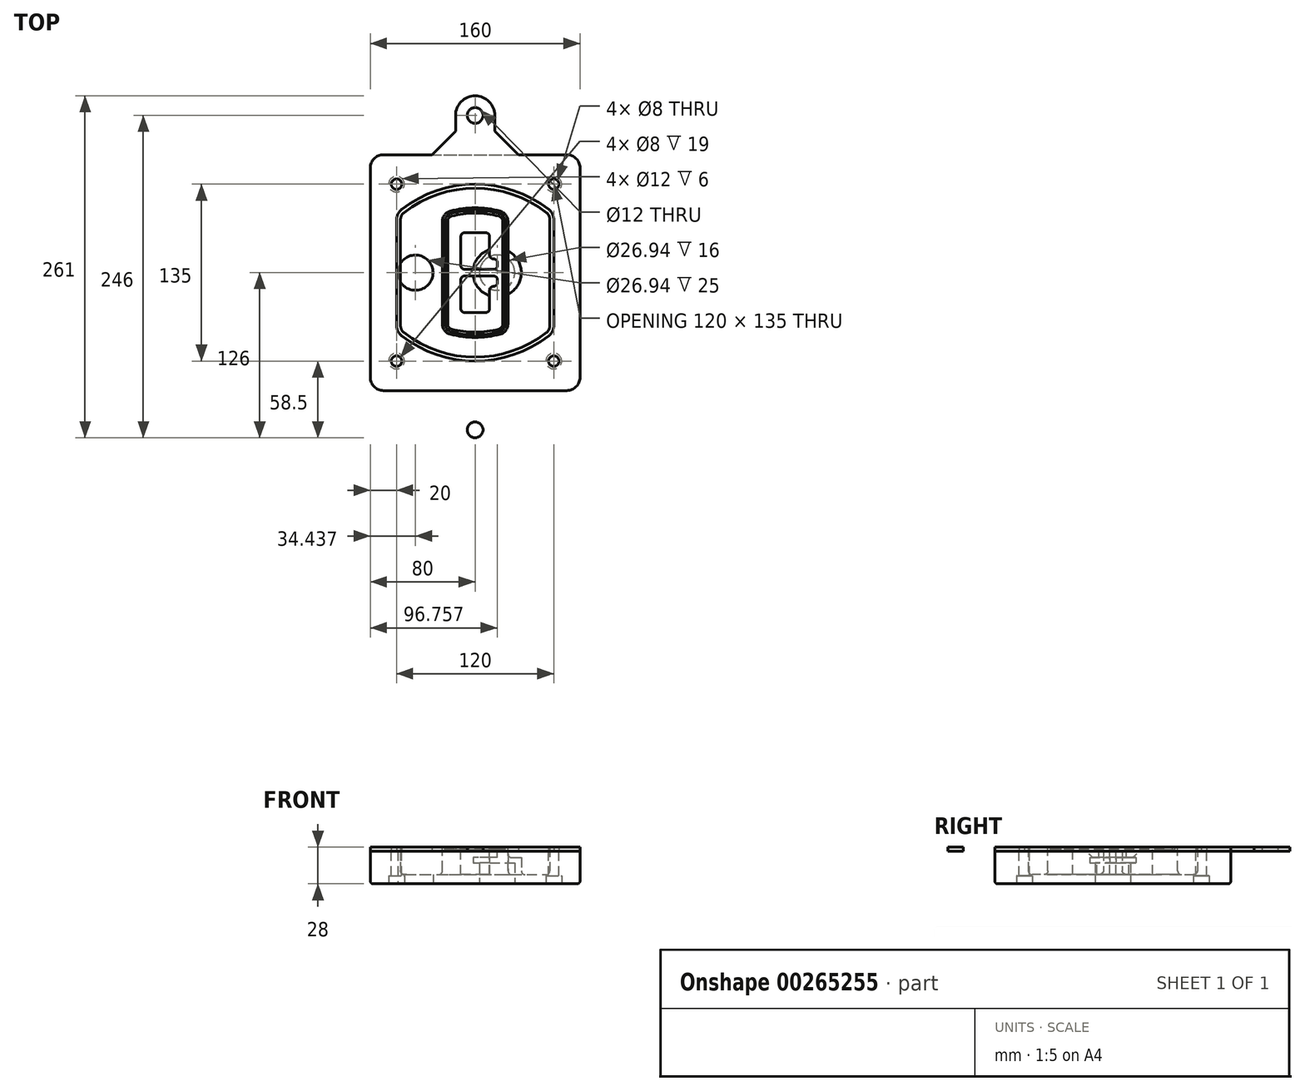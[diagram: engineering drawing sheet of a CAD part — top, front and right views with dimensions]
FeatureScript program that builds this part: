
annotation { "Feature Type Name" : "Feature", "Feature Type Description" : "" }
export const myFeature = defineFeature(function(context is Context, id is Id, definition is map)
    precondition{}
    {
        {
            var Q0;
            Q0=qCreatedBy(makeId("Top.planeOp"),FACE);
            var sketch = newSketch(context, id + "F0", { "sketchPlane" : qUnion([Q0])});
            skPoint(sketch, "E0.rect.middle", {"position": v(0, 0) * mm});
            skLineSegment(sketch, "E1.bottom", {"start": v(-70, -90) * mm, "end": v(70, -90) * mm});
            skLineSegment(sketch, "E1.top", {"start": v(-70, 90) * mm, "end": v(70, 90) * mm});
            skLineSegment(sketch, "E1.left", {"start": v(-80, -80) * mm, "end": v(-80, 80) * mm});
            skLineSegment(sketch, "E1.right", {"start": v(80, -80) * mm, "end": v(80, 80) * mm});
            skLineSegment(sketch, "E2", {"start": v(-80, 90) * mm, "end": v(80, -90) * mm, "construction": true});
            skLineSegment(sketch, "E3", {"start": v(80, 90) * mm, "end": v(-80, -90) * mm, "construction": true});
            skCircle(sketch, "E4", {"center": v(-60, 67.5) * mm, "radius": 4 * mm});
            skCircle(sketch, "E5", {"center": v(60, 67.5) * mm, "radius": 4 * mm});
            skCircle(sketch, "E6", {"center": v(60, -67.5) * mm, "radius": 4 * mm});
            skCircle(sketch, "E7", {"center": v(-60, -67.5) * mm, "radius": 4 * mm});
            skLineSegment(sketch, "E8", {"start": v(-60, 67.5) * mm, "end": v(60, 67.5) * mm, "construction": true});
            skLineSegment(sketch, "E9", {"start": v(60, 67.5) * mm, "end": v(60, -67.5) * mm, "construction": true});
            skLineSegment(sketch, "E10", {"start": v(60, -67.5) * mm, "end": v(-60, -67.5) * mm, "construction": true});
            skLineSegment(sketch, "E11", {"start": v(-60, -67.5) * mm, "end": v(-60, 67.5) * mm, "construction": true});
            skLineSegment(sketch, "E12", {"start": v(-60, 40.3) * mm, "end": v(-60, -40.3) * mm});
            skLineSegment(sketch, "E13", {"start": v(60, 40.3) * mm, "end": v(60, -40.3) * mm});
            skArc(sketch, "E14", {"start": v(56.15, 48.18) * mm, "mid": v(0, 67.5) * mm, "end": v(-56.15, 48.18) * mm});
            skArc(sketch, "E15", {"start": v(-56.15, -48.18) * mm, "mid": v(0, -67.5) * mm, "end": v(56.15, -48.18) * mm});
            skLineSegment(sketch, "E16", {"start": v(-60, 0) * mm, "end": v(60, 0) * mm, "construction": true});
            skPoint(sketch, "E17.visualSharp", {"position": v(-60, -45) * mm});
            skArc(sketch, "E17.filletArc", {"start": v(-60, -40.3) * mm, "mid": v(-58.99, -44.68) * mm, "end": v(-56.15, -48.18) * mm});
            skPoint(sketch, "E18.visualSharp", {"position": v(-60, 45) * mm});
            skArc(sketch, "E18.filletArc", {"start": v(-56.15, 48.18) * mm, "mid": v(-58.99, 44.68) * mm, "end": v(-60, 40.3) * mm});
            skPoint(sketch, "E19.visualSharp", {"position": v(60, 45) * mm});
            skArc(sketch, "E19.filletArc", {"start": v(60, 40.3) * mm, "mid": v(58.99, 44.68) * mm, "end": v(56.15, 48.18) * mm});
            skPoint(sketch, "E20.visualSharp", {"position": v(60, -45) * mm});
            skArc(sketch, "E20.filletArc", {"start": v(56.15, -48.18) * mm, "mid": v(58.99, -44.68) * mm, "end": v(60, -40.3) * mm});
            skPoint(sketch, "E21.visualSharp", {"position": v(-80, 90) * mm});
            skArc(sketch, "E21.filletArc", {"start": v(-70, 90) * mm, "mid": v(-77.07, 87.07) * mm, "end": v(-80, 80) * mm});
            skPoint(sketch, "E22.visualSharp", {"position": v(80, 90) * mm});
            skArc(sketch, "E22.filletArc", {"start": v(80, 80) * mm, "mid": v(77.07, 87.07) * mm, "end": v(70, 90) * mm});
            skPoint(sketch, "E23.visualSharp", {"position": v(80, -90) * mm});
            skArc(sketch, "E23.filletArc", {"start": v(70, -90) * mm, "mid": v(77.07, -87.07) * mm, "end": v(80, -80) * mm});
            skPoint(sketch, "E24.visualSharp", {"position": v(-80, -90) * mm});
            skArc(sketch, "E24.filletArc", {"start": v(-80, -80) * mm, "mid": v(-77.07, -87.07) * mm, "end": v(-70, -90) * mm});
            skArc(sketch, "E25.0", {"start": v(57, 40.3) * mm, "mid": v(56.3, 43.36) * mm, "end": v(54.3, 45.81) * mm});
            skLineSegment(sketch, "E25.1", {"start": v(57, 40.3) * mm, "end": v(57, -40.3) * mm});
            skArc(sketch, "E25.2", {"start": v(54.3, -45.81) * mm, "mid": v(56.3, -43.36) * mm, "end": v(57, -40.3) * mm});
            skArc(sketch, "E25.3", {"start": v(-54.3, -45.81) * mm, "mid": v(0, -64.5) * mm, "end": v(54.3, -45.81) * mm});
            skArc(sketch, "E25.4", {"start": v(-57, -40.3) * mm, "mid": v(-56.3, -43.36) * mm, "end": v(-54.3, -45.81) * mm});
            skArc(sketch, "E25.5", {"start": v(54.3, 45.81) * mm, "mid": v(0, 64.5) * mm, "end": v(-54.3, 45.81) * mm});
            skLineSegment(sketch, "E25.6", {"start": v(-57, 40.3) * mm, "end": v(-57, -40.3) * mm});
            skArc(sketch, "E25.7", {"start": v(-54.3, 45.81) * mm, "mid": v(-56.3, 43.36) * mm, "end": v(-57, 40.3) * mm});
            skArc(sketch, "E26.0", {"start": v(-58.62, 51.33) * mm, "mid": v(-62.58, 46.43) * mm, "end": v(-64, 40.3) * mm});
            skArc(sketch, "E26.1", {"start": v(58.62, 51.33) * mm, "mid": v(0, 71.5) * mm, "end": v(-58.62, 51.33) * mm});
            skArc(sketch, "E26.2", {"start": v(64, 40.3) * mm, "mid": v(62.58, 46.43) * mm, "end": v(58.62, 51.33) * mm});
            skLineSegment(sketch, "E26.3", {"start": v(64, 40.3) * mm, "end": v(64, -40.3) * mm});
            skArc(sketch, "E26.4", {"start": v(58.62, -51.33) * mm, "mid": v(62.58, -46.43) * mm, "end": v(64, -40.3) * mm});
            skLineSegment(sketch, "E26.5", {"start": v(-64, 40.3) * mm, "end": v(-64, -40.3) * mm});
            skArc(sketch, "E26.6", {"start": v(-58.62, -51.33) * mm, "mid": v(0, -71.5) * mm, "end": v(58.62, -51.33) * mm});
            skArc(sketch, "E26.7", {"start": v(-64, -40.3) * mm, "mid": v(-62.58, -46.43) * mm, "end": v(-58.62, -51.33) * mm});
            skSolve(sketch);
        }
        {
            var Q0;
            Q0=makeQuery(id+"F0.imprint","IMPRINT",FACE,{"disambiguationData":[TD([[makeQuery(id+"F0.imprint","IMPRINT",EDGE,{"derivedFrom":sQuery(id+"F0.wireOp",EDGE,"E1.bottom")}),1.0]])]});
            var Q1;
            Q1=makeQuery(id+"F0.imprint","IMPRINT",FACE,{"disambiguationData":[TD([[makeQuery(id+"F0.imprint","IMPRINT",EDGE,{"derivedFrom":sQuery(id+"F0.wireOp",EDGE,"E12")}),1.0]])]});
            var Q2;
            Q2=makeQuery(id+"F0.imprint","IMPRINT",FACE,{"disambiguationData":[TD([[makeQuery(id+"F0.imprint","IMPRINT",EDGE,{"derivedFrom":sQuery(id+"F0.wireOp",EDGE,"E25.0")}),1.0]])]});
            var Q3;
            Q3=makeQuery(id+"F0.imprint","IMPRINT",FACE,{"disambiguationData":[TD([[makeQuery(id+"F0.imprint","IMPRINT",EDGE,{"derivedFrom":sQuery(id+"F0.wireOp",EDGE,"E12")}),-1.0]])]});
            extrude(context, id + "F1", {"entities" : qUnion([Q0, Q1, Q2, Q3]), "oppositeDirection" : true, "depth" : 25 * mm});
        }
        {
            var Q0;
            Q0=makeQuery(id+"F0.imprint","IMPRINT",FACE,{"disambiguationData":[TD([[makeQuery(id+"F0.imprint","IMPRINT",EDGE,{"derivedFrom":sQuery(id+"F0.wireOp",EDGE,"E12")}),1.0]])]});
            extrude(context, id + "F2", {"entities" : qUnion([Q0]), "operationType" : NewBodyOperationType.ADD, "depth" : 3 * mm});
        }
        {
            var Q0;
            Q0=makeQuery(id+"F0.imprint","IMPRINT",FACE,{"disambiguationData":[TD([[makeQuery(id+"F0.imprint","IMPRINT",EDGE,{"derivedFrom":sQuery(id+"F0.wireOp",EDGE,"E25.0")}),1.0]])]});
            extrude(context, id + "F3", {"entities" : qUnion([Q0]), "operationType" : NewBodyOperationType.REMOVE, "oppositeDirection" : true, "depth" : 18 * mm});
        }
        {
            var Q0;
            Q0=makeQuery(id+"F2.opExtrude","CAP_FACE",FACE,{"disambiguationData":[OSD([sQuery(id+"F0.wireOp",EDGE,"E12"),sQuery(id+"F0.wireOp",EDGE,"E13"),sQuery(id+"F0.wireOp",EDGE,"E14"),sQuery(id+"F0.wireOp",EDGE,"E15"),sQuery(id+"F0.wireOp",EDGE,"E17.filletArc"),sQuery(id+"F0.wireOp",EDGE,"E18.filletArc"),sQuery(id+"F0.wireOp",EDGE,"E19.filletArc"),sQuery(id+"F0.wireOp",EDGE,"E20.filletArc"),sQuery(id+"F0.wireOp",EDGE,"E25.0"),sQuery(id+"F0.wireOp",EDGE,"E25.1"),sQuery(id+"F0.wireOp",EDGE,"E25.2"),sQuery(id+"F0.wireOp",EDGE,"E25.3"),sQuery(id+"F0.wireOp",EDGE,"E25.4"),sQuery(id+"F0.wireOp",EDGE,"E25.5"),sQuery(id+"F0.wireOp",EDGE,"E25.6"),sQuery(id+"F0.wireOp",EDGE,"E25.7")])],"isStart":false});
            var sketch = newSketch(context, id + "F4", { "sketchPlane" : qUnion([Q0])});
            skArc(sketch, "E27.0", {"start": v(-19.08, -46.97) * mm, "mid": v(0, -49.5) * mm, "end": v(19.08, -46.97) * mm});
            skArc(sketch, "E28.0", {"start": v(19.08, 46.97) * mm, "mid": v(0, 49.5) * mm, "end": v(-19.08, 46.97) * mm});
            skLineSegment(sketch, "E29", {"start": v(-25, 39.25) * mm, "end": v(-25, -39.25) * mm});
            skLineSegment(sketch, "E30", {"start": v(25, 39.25) * mm, "end": v(25, -39.25) * mm});
            skLineSegment(sketch, "E31", {"start": v(-25, 45.1) * mm, "end": v(25, 45.1) * mm, "construction": true});
            skLineSegment(sketch, "E32", {"start": v(-25, -45.1) * mm, "end": v(25, -45.1) * mm, "construction": true});
            skPoint(sketch, "E33.visualSharp", {"position": v(-25, 45.1) * mm});
            skArc(sketch, "E33.filletArc", {"start": v(-19.08, 46.97) * mm, "mid": v(-23.35, 44.11) * mm, "end": v(-25, 39.25) * mm});
            skPoint(sketch, "E34.visualSharp", {"position": v(25, 45.1) * mm});
            skArc(sketch, "E34.filletArc", {"start": v(25, 39.25) * mm, "mid": v(23.35, 44.11) * mm, "end": v(19.08, 46.97) * mm});
            skPoint(sketch, "E35.visualSharp", {"position": v(25, -45.1) * mm});
            skArc(sketch, "E35.filletArc", {"start": v(19.08, -46.97) * mm, "mid": v(23.35, -44.11) * mm, "end": v(25, -39.25) * mm});
            skPoint(sketch, "E36.visualSharp", {"position": v(-25, -45.1) * mm});
            skArc(sketch, "E36.filletArc", {"start": v(-25, -39.25) * mm, "mid": v(-23.35, -44.11) * mm, "end": v(-19.08, -46.97) * mm});
            skArc(sketch, "E37.0", {"start": v(54.3, 45.81) * mm, "mid": v(0, 64.5) * mm, "end": v(-54.3, 45.81) * mm});
            skArc(sketch, "E37.1", {"start": v(-54.3, 45.81) * mm, "mid": v(-56.3, 43.36) * mm, "end": v(-57, 40.3) * mm});
            skLineSegment(sketch, "E37.2", {"start": v(-57, 40.3) * mm, "end": v(-57, -40.3) * mm});
            skArc(sketch, "E37.3", {"start": v(-57, -40.3) * mm, "mid": v(-56.3, -43.36) * mm, "end": v(-54.3, -45.81) * mm});
            skArc(sketch, "E37.4", {"start": v(-54.3, -45.81) * mm, "mid": v(0, -64.5) * mm, "end": v(54.3, -45.81) * mm});
            skArc(sketch, "E37.5", {"start": v(54.3, -45.81) * mm, "mid": v(56.3, -43.36) * mm, "end": v(57, -40.3) * mm});
            skLineSegment(sketch, "E37.6", {"start": v(57, 40.3) * mm, "end": v(57, -40.3) * mm});
            skArc(sketch, "E37.7", {"start": v(57, 40.3) * mm, "mid": v(56.3, 43.36) * mm, "end": v(54.3, 45.81) * mm});
            skLineSegment(sketch, "E38.0", {"start": v(23, 39.25) * mm, "end": v(23, -39.25) * mm});
            skArc(sketch, "E38.1", {"start": v(18.56, -45.04) * mm, "mid": v(21.76, -42.9) * mm, "end": v(23, -39.25) * mm});
            skArc(sketch, "E38.2", {"start": v(-18.56, -45.04) * mm, "mid": v(0, -47.5) * mm, "end": v(18.56, -45.04) * mm});
            skArc(sketch, "E38.3", {"start": v(-23, -39.25) * mm, "mid": v(-21.76, -42.9) * mm, "end": v(-18.56, -45.04) * mm});
            skLineSegment(sketch, "E38.4", {"start": v(-23, 39.25) * mm, "end": v(-23, -39.25) * mm});
            skArc(sketch, "E38.5", {"start": v(23, 39.25) * mm, "mid": v(21.76, 42.9) * mm, "end": v(18.56, 45.04) * mm});
            skArc(sketch, "E38.6", {"start": v(-18.56, 45.04) * mm, "mid": v(-21.76, 42.9) * mm, "end": v(-23, 39.25) * mm});
            skArc(sketch, "E38.7", {"start": v(18.56, 45.04) * mm, "mid": v(0, 47.5) * mm, "end": v(-18.56, 45.04) * mm});
            skArc(sketch, "E39.0", {"start": v(21, 39.25) * mm, "mid": v(20.18, 41.68) * mm, "end": v(18.04, 43.1) * mm});
            skLineSegment(sketch, "E39.1", {"start": v(21, 39.25) * mm, "end": v(21, -39.25) * mm});
            skArc(sketch, "E39.2", {"start": v(18.04, -43.1) * mm, "mid": v(20.18, -41.68) * mm, "end": v(21, -39.25) * mm});
            skArc(sketch, "E39.3", {"start": v(-18.04, -43.1) * mm, "mid": v(0, -45.5) * mm, "end": v(18.04, -43.1) * mm});
            skArc(sketch, "E39.4", {"start": v(-21, -39.25) * mm, "mid": v(-20.18, -41.68) * mm, "end": v(-18.04, -43.1) * mm});
            skArc(sketch, "E39.5", {"start": v(18.04, 43.1) * mm, "mid": v(0, 45.5) * mm, "end": v(-18.04, 43.1) * mm});
            skLineSegment(sketch, "E39.6", {"start": v(-21, 39.25) * mm, "end": v(-21, -39.25) * mm});
            skArc(sketch, "E39.7", {"start": v(-18.04, 43.1) * mm, "mid": v(-20.18, 41.68) * mm, "end": v(-21, 39.25) * mm});
            skLineSegment(sketch, "E40", {"start": v(-25, 0) * mm, "end": v(25, 0) * mm, "construction": true});
            skLineSegment(sketch, "E41", {"start": v(-11, 5.5) * mm, "end": v(-11, 27.5) * mm});
            skLineSegment(sketch, "E42", {"start": v(-8, 30.5) * mm, "end": v(8, 30.5) * mm});
            skLineSegment(sketch, "E43", {"start": v(11, 27.5) * mm, "end": v(11, 13.5) * mm});
            skLineSegment(sketch, "E44", {"start": v(14, 10.5) * mm, "end": v(14, 10.5) * mm});
            skLineSegment(sketch, "E45", {"start": v(17, 7.5) * mm, "end": v(17, 5.5) * mm});
            skLineSegment(sketch, "E46", {"start": v(14, 2.5) * mm, "end": v(-8, 2.5) * mm});
            skPoint(sketch, "E47.visualSharp", {"position": v(-11, 30.5) * mm});
            skArc(sketch, "E47.filletArc", {"start": v(-8, 30.5) * mm, "mid": v(-10.12, 29.62) * mm, "end": v(-11, 27.5) * mm});
            skPoint(sketch, "E48.visualSharp", {"position": v(11, 30.5) * mm});
            skArc(sketch, "E48.filletArc", {"start": v(11, 27.5) * mm, "mid": v(10.12, 29.62) * mm, "end": v(8, 30.5) * mm});
            skPoint(sketch, "E49.visualSharp", {"position": v(11, 10.5) * mm});
            skArc(sketch, "E49.filletArc", {"start": v(11, 13.5) * mm, "mid": v(11.88, 11.38) * mm, "end": v(14, 10.5) * mm});
            skPoint(sketch, "E50.visualSharp", {"position": v(17, 10.5) * mm});
            skArc(sketch, "E50.filletArc", {"start": v(17, 7.5) * mm, "mid": v(16.12, 9.62) * mm, "end": v(14, 10.5) * mm});
            skPoint(sketch, "E51.visualSharp", {"position": v(17, 2.5) * mm});
            skArc(sketch, "E51.filletArc", {"start": v(14, 2.5) * mm, "mid": v(16.12, 3.38) * mm, "end": v(17, 5.5) * mm});
            skPoint(sketch, "E52.visualSharp", {"position": v(-11, 2.5) * mm});
            skArc(sketch, "E52.filletArc", {"start": v(-11, 5.5) * mm, "mid": v(-10.12, 3.38) * mm, "end": v(-8, 2.5) * mm});
            skLineSegment(sketch, "E53.0.MirrorCS", {"start": v(14, -2.5) * mm, "end": v(-8, -2.5) * mm});
            skArc(sketch, "E54.0.MirrorCS", {"start": v(-11, -5.5) * mm, "mid": v(-10.12, -3.38) * mm, "end": v(-8, -2.5) * mm});
            skLineSegment(sketch, "E55.0.MirrorCS", {"start": v(-11, -5.5) * mm, "end": v(-11, -27.5) * mm});
            skArc(sketch, "E56.0.MirrorCS", {"start": v(-8, -30.5) * mm, "mid": v(-10.12, -29.62) * mm, "end": v(-11, -27.5) * mm});
            skLineSegment(sketch, "E57.0.MirrorCS", {"start": v(-8, -30.5) * mm, "end": v(8, -30.5) * mm});
            skArc(sketch, "E58.0.MirrorCS", {"start": v(11, -27.5) * mm, "mid": v(10.12, -29.62) * mm, "end": v(8, -30.5) * mm});
            skLineSegment(sketch, "E59.0.MirrorCS", {"start": v(11, -27.5) * mm, "end": v(11, -13.5) * mm});
            skArc(sketch, "E60.0.MirrorCS", {"start": v(11, -13.5) * mm, "mid": v(11.88, -11.38) * mm, "end": v(14, -10.5) * mm});
            skArc(sketch, "E61.0.MirrorCS", {"start": v(17, -7.5) * mm, "mid": v(16.12, -9.62) * mm, "end": v(14, -10.5) * mm});
            skLineSegment(sketch, "E62.0.MirrorCS", {"start": v(17, -7.5) * mm, "end": v(17, -5.5) * mm});
            skArc(sketch, "E63.0.MirrorCS", {"start": v(14, -2.5) * mm, "mid": v(16.12, -3.38) * mm, "end": v(17, -5.5) * mm});
            skSolve(sketch);
        }
        {
            var Q0;
            Q0=makeQuery(id+"F4.imprint","IMPRINT",FACE,{"disambiguationData":[TD([[makeQuery(id+"F4.imprint","IMPRINT",EDGE,{"derivedFrom":sQuery(id+"F4.wireOp",EDGE,"E27.0")}),1.0]])]});
            var Q1;
            Q1=makeQuery(id+"F4.imprint","IMPRINT",FACE,{"disambiguationData":[TD([[makeQuery(id+"F4.imprint","IMPRINT",EDGE,{"derivedFrom":sQuery(id+"F4.wireOp",EDGE,"E38.0")}),-1.0]])]});
            var Q2;
            Q2=makeQuery(id+"F4.imprint","IMPRINT",FACE,{"disambiguationData":[TD([[makeQuery(id+"F4.imprint","IMPRINT",EDGE,{"derivedFrom":sQuery(id+"F4.wireOp",EDGE,"E39.0")}),1.0]])]});
            extrude(context, id + "F5", {"entities" : qUnion([Q0, Q1, Q2]), "operationType" : NewBodyOperationType.ADD, "endBound" : BoundingType.UP_TO_NEXT, "oppositeDirection" : true, "depth" : 25 * mm});
        }
        {
            var Q0;
            Q0=makeQuery(id+"F4.imprint","IMPRINT",FACE,{"disambiguationData":[TD([[makeQuery(id+"F4.imprint","IMPRINT",EDGE,{"derivedFrom":sQuery(id+"F4.wireOp",EDGE,"E38.0")}),-1.0]])]});
            extrude(context, id + "F6", {"entities" : qUnion([Q0]), "operationType" : NewBodyOperationType.REMOVE, "oppositeDirection" : true, "depth" : 2 * mm});
        }
        {
            var Q0;
            Q0=makeQuery(id+"F1.opExtrude","CAP_FACE",FACE,{"disambiguationData":[OSD([sQuery(id+"F0.wireOp",EDGE,"E1.bottom"),sQuery(id+"F0.wireOp",EDGE,"E1.top"),sQuery(id+"F0.wireOp",EDGE,"E1.left"),sQuery(id+"F0.wireOp",EDGE,"E1.right"),sQuery(id+"F0.wireOp",EDGE,"E4"),sQuery(id+"F0.wireOp",EDGE,"E5"),sQuery(id+"F0.wireOp",EDGE,"E6"),sQuery(id+"F0.wireOp",EDGE,"E7"),sQuery(id+"F0.wireOp",EDGE,"E21.filletArc"),sQuery(id+"F0.wireOp",EDGE,"E22.filletArc"),sQuery(id+"F0.wireOp",EDGE,"E23.filletArc"),sQuery(id+"F0.wireOp",EDGE,"E24.filletArc")])],"isStart":false});
            var sketch = newSketch(context, id + "F7", { "sketchPlane" : qUnion([Q0])});
            skCircle(sketch, "E64", {"center": v(16.76, 0) * mm, "radius": 13.47 * mm});
            skCircle(sketch, "E65", {"center": v(-45.56, 0) * mm, "radius": 13.47 * mm});
            skLineSegment(sketch, "E66", {"start": v(80, 0) * mm, "end": v(-80, 0) * mm});
            skCircle(sketch, "E67", {"center": v(16.76, 0) * mm, "radius": 18.47 * mm});
            skCircle(sketch, "E68", {"center": v(60, -67.5) * mm, "radius": 6 * mm});
            skCircle(sketch, "E69", {"center": v(-60, -67.5) * mm, "radius": 6 * mm});
            skCircle(sketch, "E70", {"center": v(-60, 67.5) * mm, "radius": 6 * mm});
            skCircle(sketch, "E71", {"center": v(60, 67.5) * mm, "radius": 6 * mm});
            skSolve(sketch);
        }
        {
            var Q0;
            {var subQ1=sQuery(id+"F7.wireOp",EDGE,"E66");var subQ4=sQuery(id+"F7.wireOp",EDGE,"E64");var subQ6=makeQuery(id+"F7.imprint","INTERSECT",VERTEX,{"disambiguationData":[OD(0.0)],"derivedFrom":[subQ4,subQ1]});Q0=makeQuery(id+"F7.imprint","IMPRINT",FACE,{"disambiguationData":[TD([[makeQuery(id+"F7.imprint","IMPRINT",EDGE,{"disambiguationData":[TD([[subQ6,-1.0]])],"derivedFrom":subQ4}),-1.0]])]});}
            var Q1;
            {var subQ0=sQuery(id+"F7.wireOp",EDGE,"E66");var subQ1=sQuery(id+"F7.wireOp",EDGE,"E64");var subQ3=makeQuery(id+"F7.imprint","INTERSECT",VERTEX,{"disambiguationData":[OD(0.0)],"derivedFrom":[subQ1,subQ0]});Q1=makeQuery(id+"F7.imprint","IMPRINT",FACE,{"disambiguationData":[TD([[makeQuery(id+"F7.imprint","IMPRINT",EDGE,{"disambiguationData":[TD([[subQ3,-1.0]])],"derivedFrom":subQ1}),1.0]])]});}
            var Q2;
            {var subQ0=sQuery(id+"F7.wireOp",EDGE,"E66");var subQ1=sQuery(id+"F7.wireOp",EDGE,"E64");var subQ3=makeQuery(id+"F7.imprint","INTERSECT",VERTEX,{"disambiguationData":[OD(0.0)],"derivedFrom":[subQ1,subQ0]});Q2=makeQuery(id+"F7.imprint","IMPRINT",FACE,{"disambiguationData":[TD([[makeQuery(id+"F7.imprint","IMPRINT",EDGE,{"disambiguationData":[TD([[subQ3,1.0]])],"derivedFrom":subQ1}),1.0]])]});}
            var Q3;
            {var subQ1=sQuery(id+"F7.wireOp",EDGE,"E66");var subQ4=sQuery(id+"F7.wireOp",EDGE,"E64");var subQ6=makeQuery(id+"F7.imprint","INTERSECT",VERTEX,{"disambiguationData":[OD(0.0)],"derivedFrom":[subQ4,subQ1]});Q3=makeQuery(id+"F7.imprint","IMPRINT",FACE,{"disambiguationData":[TD([[makeQuery(id+"F7.imprint","IMPRINT",EDGE,{"disambiguationData":[TD([[subQ6,1.0]])],"derivedFrom":subQ4}),-1.0]])]});}
            extrude(context, id + "F8", {"entities" : qUnion([Q0, Q1, Q2, Q3]), "operationType" : NewBodyOperationType.ADD, "oppositeDirection" : true, "depth" : 20 * mm});
        }
        {
            var Q0;
            {var subQ0=sQuery(id+"F7.wireOp",EDGE,"E66");var subQ1=sQuery(id+"F7.wireOp",EDGE,"E64");var subQ3=makeQuery(id+"F7.imprint","INTERSECT",VERTEX,{"disambiguationData":[OD(0.0)],"derivedFrom":[subQ1,subQ0]});Q0=makeQuery(id+"F7.imprint","IMPRINT",FACE,{"disambiguationData":[TD([[makeQuery(id+"F7.imprint","IMPRINT",EDGE,{"disambiguationData":[TD([[subQ3,-1.0]])],"derivedFrom":subQ1}),1.0]])]});}
            var Q1;
            {var subQ0=sQuery(id+"F7.wireOp",EDGE,"E66");var subQ1=sQuery(id+"F7.wireOp",EDGE,"E64");var subQ3=makeQuery(id+"F7.imprint","INTERSECT",VERTEX,{"disambiguationData":[OD(0.0)],"derivedFrom":[subQ1,subQ0]});Q1=makeQuery(id+"F7.imprint","IMPRINT",FACE,{"disambiguationData":[TD([[makeQuery(id+"F7.imprint","IMPRINT",EDGE,{"disambiguationData":[TD([[subQ3,1.0]])],"derivedFrom":subQ1}),1.0]])]});}
            extrude(context, id + "F9", {"entities" : qUnion([Q0, Q1]), "operationType" : NewBodyOperationType.REMOVE, "oppositeDirection" : true, "depth" : 16 * mm});
        }
        {
            var Q0;
            {var subQ0=sQuery(id+"F7.wireOp",EDGE,"E66");var subQ1=sQuery(id+"F7.wireOp",EDGE,"E65");var subQ3=makeQuery(id+"F7.imprint","INTERSECT",VERTEX,{"disambiguationData":[OD(0.0)],"derivedFrom":[subQ1,subQ0]});Q0=makeQuery(id+"F7.imprint","IMPRINT",FACE,{"disambiguationData":[TD([[makeQuery(id+"F7.imprint","IMPRINT",EDGE,{"disambiguationData":[TD([[subQ3,-1.0]])],"derivedFrom":subQ1}),1.0]])]});}
            var Q1;
            {var subQ0=sQuery(id+"F7.wireOp",EDGE,"E66");var subQ1=sQuery(id+"F7.wireOp",EDGE,"E65");var subQ3=makeQuery(id+"F7.imprint","INTERSECT",VERTEX,{"disambiguationData":[OD(0.0)],"derivedFrom":[subQ1,subQ0]});Q1=makeQuery(id+"F7.imprint","IMPRINT",FACE,{"disambiguationData":[TD([[makeQuery(id+"F7.imprint","IMPRINT",EDGE,{"disambiguationData":[TD([[subQ3,1.0]])],"derivedFrom":subQ1}),1.0]])]});}
            extrude(context, id + "F10", {"entities" : qUnion([Q0, Q1]), "operationType" : NewBodyOperationType.REMOVE, "oppositeDirection" : true, "depth" : 25 * mm});
        }
        {
            var Q0;
            Q0=makeQuery(id+"F7.imprint","IMPRINT",FACE,{"disambiguationData":[TD([[makeQuery(id+"F7.imprint","IMPRINT",EDGE,{"derivedFrom":sQuery(id+"F7.wireOp",EDGE,"E68")}),1.0]])]});
            var Q1;
            Q1=makeQuery(id+"F7.imprint","IMPRINT",FACE,{"disambiguationData":[TD([[makeQuery(id+"F7.imprint","IMPRINT",EDGE,{"derivedFrom":makeQuery(id+"F1.opExtrude","CAP_EDGE",EDGE,{"disambiguationData":[OSD([sQuery(id+"F0.wireOp",EDGE,"E5")])],"isStart":false})}),-1.0]])]});
            var Q2;
            Q2=makeQuery(id+"F7.imprint","IMPRINT",FACE,{"disambiguationData":[TD([[makeQuery(id+"F7.imprint","IMPRINT",EDGE,{"derivedFrom":sQuery(id+"F7.wireOp",EDGE,"E69")}),1.0]])]});
            var Q3;
            Q3=makeQuery(id+"F7.imprint","IMPRINT",FACE,{"disambiguationData":[TD([[makeQuery(id+"F7.imprint","IMPRINT",EDGE,{"derivedFrom":makeQuery(id+"F1.opExtrude","CAP_EDGE",EDGE,{"disambiguationData":[OSD([sQuery(id+"F0.wireOp",EDGE,"E4")])],"isStart":false})}),-1.0]])]});
            var Q4;
            Q4=makeQuery(id+"F7.imprint","IMPRINT",FACE,{"disambiguationData":[TD([[makeQuery(id+"F7.imprint","IMPRINT",EDGE,{"derivedFrom":sQuery(id+"F7.wireOp",EDGE,"E70")}),1.0]])]});
            var Q5;
            Q5=makeQuery(id+"F7.imprint","IMPRINT",FACE,{"disambiguationData":[TD([[makeQuery(id+"F7.imprint","IMPRINT",EDGE,{"derivedFrom":makeQuery(id+"F1.opExtrude","CAP_EDGE",EDGE,{"disambiguationData":[OSD([sQuery(id+"F0.wireOp",EDGE,"E7")])],"isStart":false})}),-1.0]])]});
            var Q6;
            Q6=makeQuery(id+"F7.imprint","IMPRINT",FACE,{"disambiguationData":[TD([[makeQuery(id+"F7.imprint","IMPRINT",EDGE,{"derivedFrom":sQuery(id+"F7.wireOp",EDGE,"E71")}),1.0]])]});
            var Q7;
            Q7=makeQuery(id+"F7.imprint","IMPRINT",FACE,{"disambiguationData":[TD([[makeQuery(id+"F7.imprint","IMPRINT",EDGE,{"derivedFrom":makeQuery(id+"F1.opExtrude","CAP_EDGE",EDGE,{"disambiguationData":[OSD([sQuery(id+"F0.wireOp",EDGE,"E6")])],"isStart":false})}),-1.0]])]});
            extrude(context, id + "F11", {"entities" : qUnion([Q0, Q1, Q2, Q3, Q4, Q5, Q6, Q7]), "operationType" : NewBodyOperationType.REMOVE, "oppositeDirection" : true, "depth" : 6 * mm});
        }
        {
            var Q0;
            Q0=makeQuery(id+"F9.boolean.opBoolean","COPY",FACE,{"derivedFrom":makeQuery(id+"F9.opExtrude","CAP_FACE",FACE,{"disambiguationData":[OSD([sQuery(id+"F7.wireOp",EDGE,"E64")])],"isStart":false})});
            var sketch = newSketch(context, id + "F12", { "sketchPlane" : qUnion([Q0])});
            skArc(sketch, "E72.0", {"start": v(11, 17.55) * mm, "mid": v(2.57, 11.82) * mm, "end": v(-1.54, 2.5) * mm});
            skArc(sketch, "E72.1", {"start": v(-1.54, -2.5) * mm, "mid": v(2.57, -11.82) * mm, "end": v(11, -17.55) * mm});
            skLineSegment(sketch, "E73", {"start": v(-1.54, -2.5) * mm, "end": v(14, -2.5) * mm});
            skLineSegment(sketch, "E74.0", {"start": v(14, 2.5) * mm, "end": v(-1.54, 2.5) * mm});
            skArc(sketch, "E74.1", {"start": v(14, 2.5) * mm, "mid": v(16.12, 3.38) * mm, "end": v(17, 5.5) * mm});
            skLineSegment(sketch, "E74.2", {"start": v(17, 7.5) * mm, "end": v(17, 5.5) * mm});
            skArc(sketch, "E74.3", {"start": v(17, 7.5) * mm, "mid": v(16.12, 9.62) * mm, "end": v(14, 10.5) * mm});
            skArc(sketch, "E74.4", {"start": v(11, 13.5) * mm, "mid": v(11.88, 11.38) * mm, "end": v(14, 10.5) * mm});
            skLineSegment(sketch, "E74.5", {"start": v(11, 17.55) * mm, "end": v(11, 13.5) * mm});
            skLineSegment(sketch, "E74.7", {"start": v(14, -2.5) * mm, "end": v(-1.54, -2.5) * mm});
            skArc(sketch, "E74.8", {"start": v(14, -2.5) * mm, "mid": v(16.12, -3.38) * mm, "end": v(17, -5.5) * mm});
            skLineSegment(sketch, "E74.9", {"start": v(17, -7.5) * mm, "end": v(17, -5.5) * mm});
            skArc(sketch, "E74.10", {"start": v(17, -7.5) * mm, "mid": v(16.12, -9.62) * mm, "end": v(14, -10.5) * mm});
            skArc(sketch, "E74.11", {"start": v(11, -13.5) * mm, "mid": v(11.88, -11.38) * mm, "end": v(14, -10.5) * mm});
            skLineSegment(sketch, "E74.12", {"start": v(11, -17.55) * mm, "end": v(11, -13.5) * mm});
            skPoint(sketch, "E75.orphan", {"position": v(11, -27.5) * mm});
            skPoint(sketch, "E76.orphan", {"position": v(-8, -2.5) * mm});
            skPoint(sketch, "E77.orphan", {"position": v(-8, 2.5) * mm});
            skPoint(sketch, "E78.orphan", {"position": v(11, 27.5) * mm});
            skSolve(sketch);
        }
        {
            var Q0;
            {var subQ7=sQuery(id+"F12.wireOp",EDGE,"E72.0");var subQ14=sQuery(id+"F12.wireOp",EDGE,"E72.1");var subQ16=sQuery(id+"F12.wireOp",EDGE,"E74.1");var subQ18=sQuery(id+"F12.wireOp",EDGE,"E74.8");Q0=qUnion([makeQuery(id+"F12.imprint","IMPRINT",FACE,{"disambiguationData":[TD([[makeQuery(id+"F12.imprint","IMPRINT",EDGE,{"derivedFrom":subQ7}),1.0]])]}),makeQuery(id+"F12.imprint","IMPRINT",FACE,{"disambiguationData":[TD([[makeQuery(id+"F12.imprint","IMPRINT",EDGE,{"derivedFrom":subQ14}),1.0]])]}),makeQuery(id+"F12.imprint","IMPRINT",FACE,{"disambiguationData":[TD([[makeQuery(id+"F12.imprint","IMPRINT",EDGE,{"derivedFrom":subQ16}),1.0]])]}),makeQuery(id+"F12.imprint","IMPRINT",FACE,{"disambiguationData":[TD([[makeQuery(id+"F12.imprint","IMPRINT",EDGE,{"derivedFrom":subQ18}),-1.0]])]})]);}
            var Q1;
            Q1=makeQuery(id+"F5.boolean.opBoolean","SPLIT",FACE,{"disambiguationData":[TD([makeQuery(id+"F5.opExtrude","SWEPT_FACE",FACE,{"disambiguationData":[OSD([sQuery(id+"F4.wireOp",EDGE,"E41")])]})])],"derivedFrom":makeQuery(id+"F3.boolean.opBoolean","COPY",FACE,{"derivedFrom":makeQuery(id+"F3.opExtrude","CAP_FACE",FACE,{"disambiguationData":[OSD([sQuery(id+"F0.wireOp",EDGE,"E25.0"),sQuery(id+"F0.wireOp",EDGE,"E25.1"),sQuery(id+"F0.wireOp",EDGE,"E25.2"),sQuery(id+"F0.wireOp",EDGE,"E25.3"),sQuery(id+"F0.wireOp",EDGE,"E25.4"),sQuery(id+"F0.wireOp",EDGE,"E25.5"),sQuery(id+"F0.wireOp",EDGE,"E25.6"),sQuery(id+"F0.wireOp",EDGE,"E25.7")])],"isStart":false})})});
            extrude(context, id + "F13", {"entities" : qUnion([Q0]), "operationType" : NewBodyOperationType.REMOVE, "endBound" : BoundingType.UP_TO_SURFACE, "endBoundEntityFace" : qUnion([Q1]), "depth" : 25 * mm});
        }
        {
            var Q0;
            Q0=makeQuery(id+"F3.boolean.opBoolean","COPY",EDGE,{"derivedFrom":makeQuery(id+"F3.opExtrude","CAP_EDGE",EDGE,{"disambiguationData":[OSD([sQuery(id+"F0.wireOp",EDGE,"E25.6")])],"isStart":false})});
            var Q1;
            Q1=makeQuery(id+"F8.boolean.opBoolean","INTERSECT",EDGE,{"derivedFrom":[makeQuery(id+"F5.opExtrude","SWEPT_FACE",FACE,{"disambiguationData":[OSD([sQuery(id+"F4.wireOp",EDGE,"E30")])]}),makeQuery(id+"F8.opExtrude","CAP_FACE",FACE,{"disambiguationData":[OSD([sQuery(id+"F7.wireOp",EDGE,"E67")])],"isStart":false})]});
            var Q2;
            Q2=makeQuery(id+"F8.boolean.opBoolean","INTERSECT",EDGE,{"disambiguationData":[OD(1.0)],"derivedFrom":[makeQuery(id+"F5.opExtrude","SWEPT_FACE",FACE,{"disambiguationData":[OSD([sQuery(id+"F4.wireOp",EDGE,"E30")])]}),makeQuery(id+"F8.opExtrude","SWEPT_FACE",FACE,{"disambiguationData":[OSD([sQuery(id+"F7.wireOp",EDGE,"E67")])]})]});
            var Q3;
            {var subQ0=sQuery(id+"F4.wireOp",EDGE,"E30");Q3=makeQuery(id+"F8.boolean.opBoolean","SPLIT",EDGE,{"disambiguationData":[TD([makeQuery(id+"F5.opExtrude","SWEPT_FACE",FACE,{"disambiguationData":[OSD([sQuery(id+"F4.wireOp",EDGE,"E35.filletArc")])]})])],"derivedFrom":makeQuery(id+"F5.opExtrude","CAP_EDGE",EDGE,{"disambiguationData":[OSD([subQ0])],"isStart":false})});}
            var Q4;
            {var subQ0=sQuery(id+"F0.wireOp",EDGE,"E25.7");var subQ1=sQuery(id+"F0.wireOp",EDGE,"E25.1");var subQ2=sQuery(id+"F0.wireOp",EDGE,"E25.6");var subQ3=sQuery(id+"F0.wireOp",EDGE,"E25.5");var subQ4=sQuery(id+"F0.wireOp",EDGE,"E25.4");var subQ5=sQuery(id+"F0.wireOp",EDGE,"E25.0");var subQ6=sQuery(id+"F0.wireOp",EDGE,"E25.2");var subQ7=sQuery(id+"F0.wireOp",EDGE,"E25.3");Q4=makeQuery(id+"F8.boolean.opBoolean","INTERSECT",EDGE,{"derivedFrom":[makeQuery(id+"F5.boolean.opBoolean","SPLIT",FACE,{"disambiguationData":[TD([makeQuery(id+"F2.opExtrude","SWEPT_FACE",FACE,{"disambiguationData":[OSD([subQ5])]})])],"derivedFrom":makeQuery(id+"F3.boolean.opBoolean","COPY",FACE,{"derivedFrom":makeQuery(id+"F3.opExtrude","CAP_FACE",FACE,{"disambiguationData":[OSD([subQ5,subQ1,subQ6,subQ7,subQ4,subQ3,subQ2,subQ0])],"isStart":false})})}),makeQuery(id+"F8.opExtrude","SWEPT_FACE",FACE,{"disambiguationData":[OSD([sQuery(id+"F7.wireOp",EDGE,"E67")])]})]});}
            var Q5;
            Q5=makeQuery(id+"F8.boolean.opBoolean","INTERSECT",EDGE,{"disambiguationData":[OD(0.0)],"derivedFrom":[makeQuery(id+"F5.opExtrude","SWEPT_FACE",FACE,{"disambiguationData":[OSD([sQuery(id+"F4.wireOp",EDGE,"E30")])]}),makeQuery(id+"F8.opExtrude","SWEPT_FACE",FACE,{"disambiguationData":[OSD([sQuery(id+"F7.wireOp",EDGE,"E67")])]})]});
            fillet(context, id + "F14", {"entities" : qUnion([Q0, Q1, Q2, Q3, Q4, Q5]), "radius" : 3 * mm, "tangentPropagation" : true, "allowEdgeOverflow" : false});
        }
        {
            var Q0;
            Q0=makeQuery(id+"F1.opExtrude","CAP_EDGE",EDGE,{"disambiguationData":[OSD([sQuery(id+"F0.wireOp",EDGE,"E1.bottom")])],"isStart":false});
            fillet(context, id + "F15", {"entities" : qUnion([Q0]), "radius" : 2 * mm, "tangentPropagation" : true, "allowEdgeOverflow" : false});
        }
        {
            var Q0;
            {var subQ0=sQuery(id+"F0.wireOp",EDGE,"E22.filletArc");var subQ1=sQuery(id+"F0.wireOp",EDGE,"E7");var subQ2=sQuery(id+"F0.wireOp",EDGE,"E6");var subQ3=sQuery(id+"F0.wireOp",EDGE,"E5");var subQ4=sQuery(id+"F0.wireOp",EDGE,"E4");var subQ5=sQuery(id+"F0.wireOp",EDGE,"E1.bottom");var subQ6=sQuery(id+"F0.wireOp",EDGE,"E21.filletArc");var subQ7=sQuery(id+"F0.wireOp",EDGE,"E1.top");var subQ8=sQuery(id+"F0.wireOp",EDGE,"E1.left");var subQ9=sQuery(id+"F0.wireOp",EDGE,"E1.right");var subQ10=sQuery(id+"F0.wireOp",EDGE,"E23.filletArc");var subQ11=sQuery(id+"F0.wireOp",EDGE,"E24.filletArc");Q0=makeQuery(id+"F2.boolean.opBoolean","SPLIT",FACE,{"disambiguationData":[TD([makeQuery(id+"F1.opExtrude","SWEPT_FACE",FACE,{"disambiguationData":[OSD([subQ5])]})])],"derivedFrom":makeQuery(id+"F1.opExtrude","CAP_FACE",FACE,{"disambiguationData":[OSD([subQ5,subQ7,subQ8,subQ9,subQ4,subQ3,subQ2,subQ1,subQ6,subQ0,subQ10,subQ11])],"isStart":true})});}
            var sketch = newSketch(context, id + "F16", { "sketchPlane" : qUnion([Q0])});
            skCircle(sketch, "E79", {"center": v(0, 120) * mm, "radius": 6 * mm});
            skPoint(sketch, "E79.centerSnap0", {"position": v(0, 67.5) * mm});
            skArc(sketch, "E80", {"start": v(15, 120) * mm, "mid": v(0, 135) * mm, "end": v(-15, 120) * mm});
            skLineSegment(sketch, "E81", {"start": v(-15, 120) * mm, "end": v(-15, 108) * mm});
            skLineSegment(sketch, "E82", {"start": v(15, 120) * mm, "end": v(15, 108) * mm});
            skLineSegment(sketch, "E83", {"start": v(15, 108) * mm, "end": v(33, 90) * mm});
            skLineSegment(sketch, "E84", {"start": v(-15, 108) * mm, "end": v(-33, 90) * mm});
            skLineSegment(sketch, "E85", {"start": v(-33, 90) * mm, "end": v(33, 90) * mm});
            skLineSegment(sketch, "E86.0", {"start": v(-80, -80) * mm, "end": v(-80, 80) * mm});
            skArc(sketch, "E87.0", {"start": v(-70, 90) * mm, "mid": v(-77.07, 87.07) * mm, "end": v(-80, 80) * mm});
            skLineSegment(sketch, "E87.1", {"start": v(-70, 90) * mm, "end": v(70, 90) * mm});
            skArc(sketch, "E87.2", {"start": v(80, 80) * mm, "mid": v(77.07, 87.07) * mm, "end": v(70, 90) * mm});
            skLineSegment(sketch, "E87.3", {"start": v(80, -80) * mm, "end": v(80, 80) * mm});
            skLineSegment(sketch, "E87.4", {"start": v(-70, -90) * mm, "end": v(70, -90) * mm});
            skArc(sketch, "E87.5", {"start": v(70, -90) * mm, "mid": v(77.07, -87.07) * mm, "end": v(80, -80) * mm});
            skArc(sketch, "E87.6", {"start": v(-80, -80) * mm, "mid": v(-77.07, -87.07) * mm, "end": v(-70, -90) * mm});
            skCircle(sketch, "E88.0", {"center": v(-60, 67.5) * mm, "radius": 4 * mm});
            skArc(sketch, "E88.1", {"start": v(56.15, 48.18) * mm, "mid": v(0, 67.5) * mm, "end": v(-56.15, 48.18) * mm});
            skLineSegment(sketch, "E88.2", {"start": v(-60, 40.3) * mm, "end": v(-60, -40.3) * mm});
            skArc(sketch, "E88.3", {"start": v(-56.15, 48.18) * mm, "mid": v(-58.99, 44.68) * mm, "end": v(-60, 40.3) * mm});
            skArc(sketch, "E88.4", {"start": v(-60, -40.3) * mm, "mid": v(-58.99, -44.68) * mm, "end": v(-56.15, -48.18) * mm});
            skArc(sketch, "E88.5", {"start": v(-56.15, -48.18) * mm, "mid": v(0, -67.5) * mm, "end": v(56.15, -48.18) * mm});
            skArc(sketch, "E88.6", {"start": v(56.15, -48.18) * mm, "mid": v(58.99, -44.68) * mm, "end": v(60, -40.3) * mm});
            skLineSegment(sketch, "E88.7", {"start": v(60, 40.3) * mm, "end": v(60, -40.3) * mm});
            skArc(sketch, "E88.8", {"start": v(60, 40.3) * mm, "mid": v(58.99, 44.68) * mm, "end": v(56.15, 48.18) * mm});
            skCircle(sketch, "E88.9", {"center": v(60, 67.5) * mm, "radius": 4 * mm});
            skCircle(sketch, "E88.10", {"center": v(60, -67.5) * mm, "radius": 4 * mm});
            skCircle(sketch, "E88.11", {"center": v(-60, -67.5) * mm, "radius": 4 * mm});
            skCircle(sketch, "E89.MirrorC", {"center": v(0, -120) * mm, "radius": 6 * mm});
            skArc(sketch, "E90.MirrorCS", {"start": v(15, -120) * mm, "mid": v(0, -135) * mm, "end": v(-15, -120) * mm});
            skLineSegment(sketch, "E91.MirrorCS", {"start": v(-15, -120) * mm, "end": v(-15, -108) * mm});
            skLineSegment(sketch, "E92.MirrorCS", {"start": v(15, -120) * mm, "end": v(15, -108) * mm});
            skLineSegment(sketch, "E93.MirrorCS", {"start": v(15, -108) * mm, "end": v(33, -90) * mm});
            skLineSegment(sketch, "E94.MirrorCS", {"start": v(-15, -108) * mm, "end": v(-33, -90) * mm});
            skSolve(sketch);
        }
        {
            var Q0;
            Q0=makeQuery(id+"F16.imprint","IMPRINT",FACE,{"disambiguationData":[TD([[makeQuery(id+"F16.imprint","IMPRINT",EDGE,{"derivedFrom":sQuery(id+"F16.wireOp",EDGE,"E86.0")}),-1.0]])]});
            var Q1;
            Q1=makeQuery(id+"F16.imprint","IMPRINT",FACE,{"disambiguationData":[TD([[makeQuery(id+"F16.imprint","IMPRINT",EDGE,{"derivedFrom":sQuery(id+"F16.wireOp",EDGE,"E79")}),-1.0]])]});
            var Q2;
            Q2=makeQuery(id+"F16.imprint","IMPRINT",FACE,{"disambiguationData":[TD([[makeQuery(id+"F16.imprint","IMPRINT",EDGE,{"derivedFrom":sQuery(id+"F16.wireOp",EDGE,"E89.MirrorC")}),1.0]])]});
            var Q3;
            Q3=makeQuery(id+"F2.opExtrude","CAP_FACE",FACE,{"disambiguationData":[OSD([sQuery(id+"F0.wireOp",EDGE,"E12"),sQuery(id+"F0.wireOp",EDGE,"E13"),sQuery(id+"F0.wireOp",EDGE,"E14"),sQuery(id+"F0.wireOp",EDGE,"E15"),sQuery(id+"F0.wireOp",EDGE,"E17.filletArc"),sQuery(id+"F0.wireOp",EDGE,"E18.filletArc"),sQuery(id+"F0.wireOp",EDGE,"E19.filletArc"),sQuery(id+"F0.wireOp",EDGE,"E20.filletArc"),sQuery(id+"F0.wireOp",EDGE,"E25.0"),sQuery(id+"F0.wireOp",EDGE,"E25.1"),sQuery(id+"F0.wireOp",EDGE,"E25.2"),sQuery(id+"F0.wireOp",EDGE,"E25.3"),sQuery(id+"F0.wireOp",EDGE,"E25.4"),sQuery(id+"F0.wireOp",EDGE,"E25.5"),sQuery(id+"F0.wireOp",EDGE,"E25.6"),sQuery(id+"F0.wireOp",EDGE,"E25.7")])],"isStart":false});
            extrude(context, id + "F17", {"entities" : qUnion([Q0, Q1, Q2]), "endBound" : BoundingType.UP_TO_SURFACE, "endBoundEntityFace" : qUnion([Q3]), "depth" : 25 * mm});
        }
    });
